# Revit family: Haworth_Epure_CompactDesk_Symmetrical90_EU_PRELIMINARY
name_source: partatom
category: Furniture
units: mm (PartAtom-declared; Revit-internal decimal feet)

## family parameters
Always vertical = Yes
Cut with Voids When Loaded = No
OmniClass Number = 23.40.70.14.64.11
OmniClass Title = Office Furniture
Room Calculation Point = No
Shared = No
Work Plane-Based = No

## types (8) — shared parameters
Actual Height = 73 cm
Assembly Code = E2020200
Description = Haworth - Epure - Symmetrical Compact Desk
Flip Top Finish = Haworth _ Paint _ Metallic Silver
Leg Height = 70 cm
Manufacturer = Haworth
Model = EUCOXXXXX
Revision Number = 1
Size = Verify Final Dim.w/ Haworth
Trim Finish = Haworth _ Metal _ Structured White EC
URL = https://www.haworth.com
URL - Product = https://www.haworth.com
Warranty = http://www.haworth.com

## per-type parameters (varying)
| type | Accessory Kit | Actual Depth | Actual Width | Cable Outlet | Flip Top Cable Outlet | Large | Leg Depth | Leg Width | Medium | No Accessory Kit | Round Cable Outlet | Rounded Corners | Small | Squared Corners |
| 120w x 60d - rounded | No | 120 cm | 120 cm | No | No | No | 20 cm | 2 cm | No | Yes | No | Yes | Yes | No |
| 140w x 60d - squared | Yes | 140 cm | 140 cm | No | No | No | 30 cm | 15 cm | Yes | No | Yes | No | No | Yes |
| 160w x 60d - scallop | No | 160 cm | 160 cm | No | No | Yes | 40 cm | 20 cm | No | Yes | No | Yes | No | No |
| 160w x 80d - rounded | Yes | 160 cm | 160 cm | No | Yes | Yes | 40 cm | 20 cm | No | No | No | Yes | No | No |
| 120w x 60d - squared | No | 120 cm | 120 cm | Yes | No | No | 20 cm | 2 cm | No | Yes | No | No | Yes | Yes |
| 140w x 60d - rounded | Yes | 140 cm | 140 cm | No | Yes | No | 30 cm | 15 cm | Yes | No | No | Yes | No | No |
| 160w x 60d - squared | No | 160 cm | 160 cm | Yes | No | Yes | 40 cm | 20 cm | No | Yes | No | No | No | Yes |
| 160w x 80d - squared | Yes | 160 cm | 160 cm | No | No | Yes | 40 cm | 20 cm | No | No | Yes | No | No | Yes |

type visibility flags: 8 boolean params named "<type name>" — each type sets only its own to Yes (folded from table)

## geometry (parser evidence)
native form markers: Sweep x16
no freeform markers — native parametric forms only
